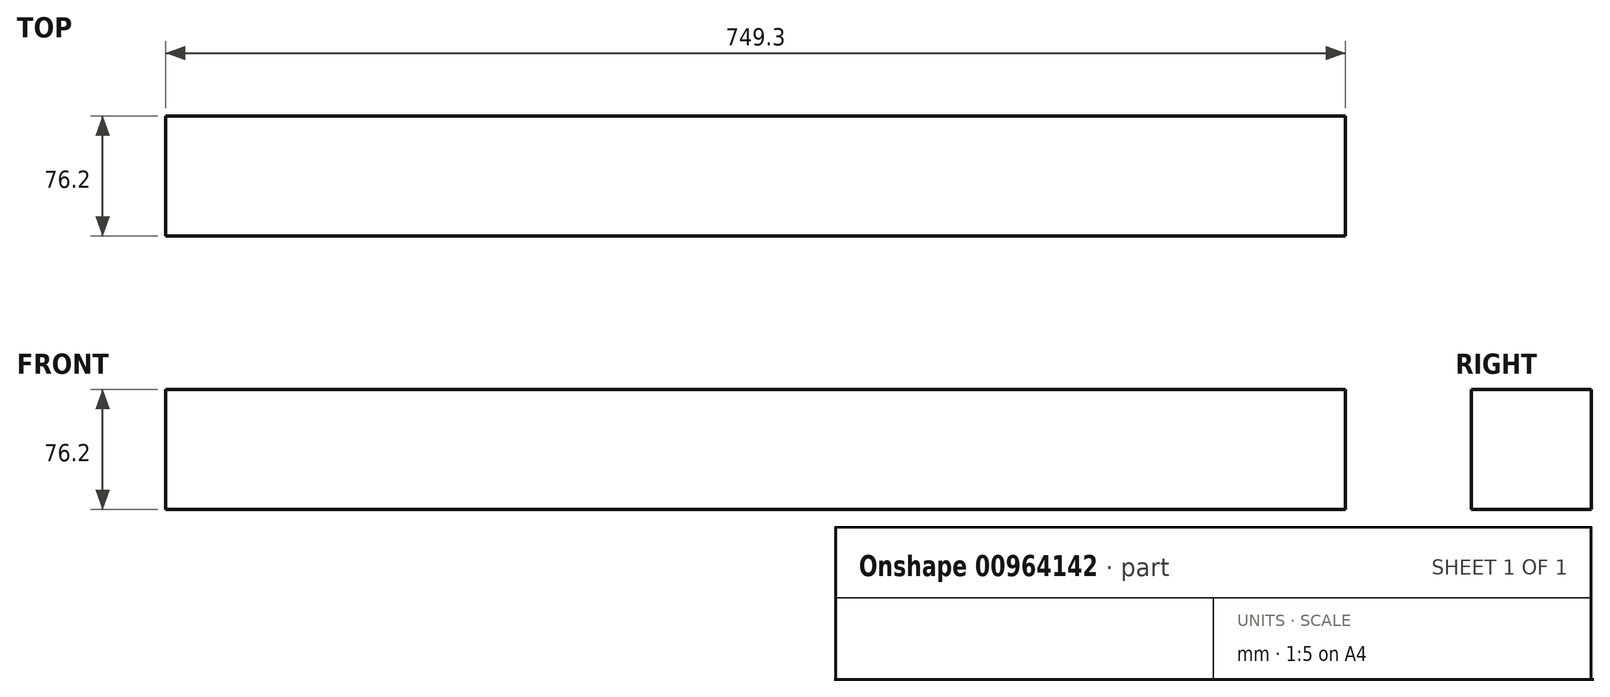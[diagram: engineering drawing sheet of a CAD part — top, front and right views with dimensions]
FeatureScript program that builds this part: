
annotation { "Feature Type Name" : "Feature", "Feature Type Description" : "" }
export const myFeature = defineFeature(function(context is Context, id is Id, definition is map)
    precondition{}
    {
        {
            var Q0;
            Q0=qCreatedBy(makeId("Top.planeOp"),FACE);
            var sketch = newSketch(context, id + "F0", { "sketchPlane" : qUnion([Q0])});
            skLineSegment(sketch, "E0.bottom", {"start": v(-143.44, 53.39) * mm, "end": v(605.86, 53.39) * mm});
            skLineSegment(sketch, "E0.top", {"start": v(-143.44, -22.81) * mm, "end": v(605.86, -22.81) * mm});
            skLineSegment(sketch, "E0.left", {"start": v(-143.44, 53.39) * mm, "end": v(-143.44, -22.81) * mm});
            skLineSegment(sketch, "E0.right", {"start": v(605.86, 53.39) * mm, "end": v(605.86, -22.81) * mm});
            skSolve(sketch);
        }
        {
            var Q0;
            Q0=makeQuery(id+"F0.imprint","IMPRINT",FACE,{"disambiguationData":[TD([[makeQuery(id+"F0.imprint","IMPRINT",EDGE,{"derivedFrom":sQuery(id+"F0.wireOp",EDGE,"E0.bottom")}),-1.0]])]});
            extrude(context, id + "F1", {"entities" : qUnion([Q0]), "depth" : 76.2 * mm, "offsetDistance" : 25.4 * mm});
        }
    });
